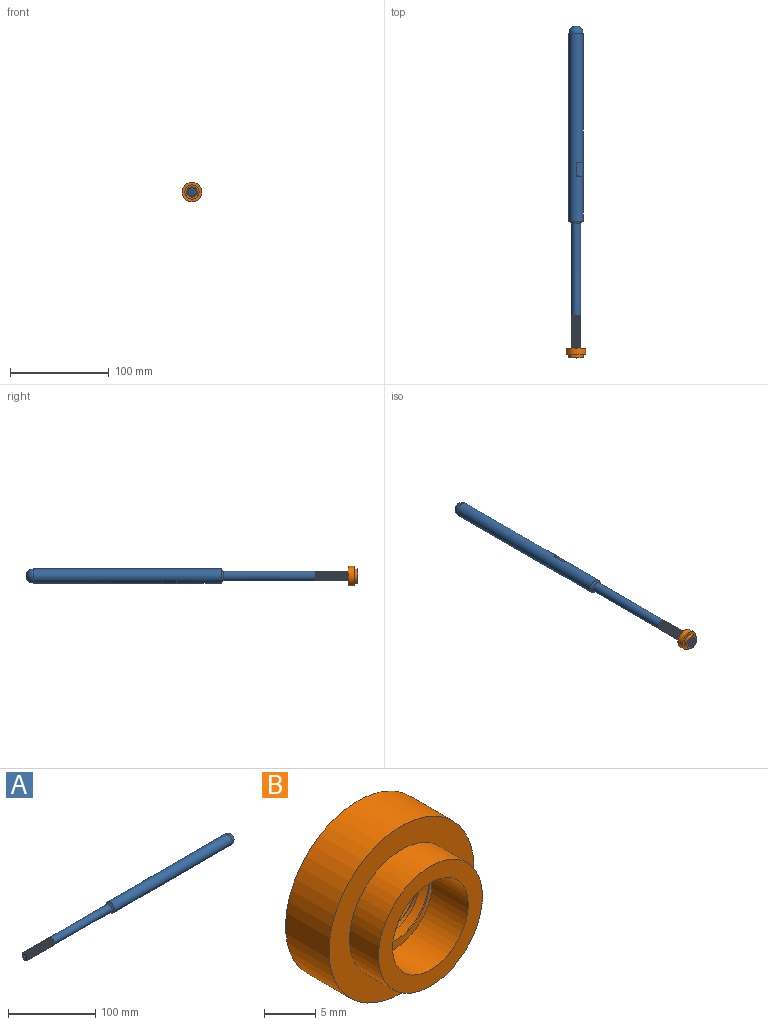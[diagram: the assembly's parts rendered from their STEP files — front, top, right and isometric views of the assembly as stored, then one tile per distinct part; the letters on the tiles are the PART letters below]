
ASSEMBLY  parts=2 mates=1
PART A: 68 faces, bbox 338x18x18 mm
  f0: cylinder r=7.15mm len=190.86mm, axis (-1,0,0), area 8339.1mm2, adj f1,f7,f8,f9,f10,f16,f17,f18
  f1: cylinder r=2.59mm len=3.79mm, axis (0,0,-1), area 0.2mm2, adj f0,f2,f9
  f2: plane 5.59x5.59mm, normal (0,0,-1), area 6.9mm2, adj f1,f3,f5,f6,f7,f8,f9
  f3: bspline ~8.22x5.92mm, area 60.7mm2, adj f2,f4,f5,f9
  f4: plane 4.64x4.63mm, normal (0,0,-1), area 14.3mm2, adj f3,f5,f6,f9
  f5: cylinder r=1.75mm len=7.15mm, axis (0,0,-1), area 19.5mm2, adj f2,f3,f4,f6
  f6: bspline ~8.22x5.92mm, area 60.7mm2, adj f2,f4,f5,f9
  f7: cylinder r=2.59mm len=5.19mm, axis (0,0,-1), area 0mm2, adj f0,f2
  f8: cylinder r=2.59mm len=4.13mm, axis (0,0,-1), area 0.9mm2, adj f0,f2,f9
  f9: bspline ~7.69x6.07mm, area 16.4mm2, adj f0,f1,f2,f3,f4,f6,f8
  f10: cylinder r=2.59mm len=3.79mm, axis (0,0,-1), area 0.2mm2, adj f0,f11,f18
  f11: plane 5.59x5.59mm, normal (0,0,-1), area 6.9mm2, adj f10,f12,f14,f15,f16,f17,f18
  f12: bspline ~8.22x5.92mm, area 60.7mm2, adj f11,f13,f14,f18
  f13: plane 4.64x4.63mm, normal (0,0,-1), area 14.3mm2, adj f12,f14,f15,f18
  f14: cylinder r=1.75mm len=7.15mm, axis (0,0,-1), area 19.5mm2, adj f11,f12,f13,f15
  f15: bspline ~8.22x5.92mm, area 60.7mm2, adj f11,f13,f14,f18
  f16: cylinder r=2.59mm len=5.19mm, axis (0,0,-1), area 0mm2, adj f0,f11
  f17: cylinder r=2.59mm len=4.13mm, axis (0,0,-1), area 0.9mm2, adj f0,f11,f18
  f18: bspline ~7.69x6.07mm, area 16.4mm2, adj f0,f10,f11,f12,f13,f15,f17
  f19: bspline ~6.29x4.05mm, area 3.6mm2, adj f0,f22
  f20: plane 0.78x0.45mm, normal (1,0,0), area 0mm2, adj f0,f21
  f21: bspline ~6.28x4.03mm, area 4mm2, adj f0,f20,f22
  f22: plane 13.19x5.39mm, normal (0,-0.87,-0.5), area 82.1mm2, adj f0,f19,f21
  f23: sphere r=7.15mm, area 320.8mm2, adj f0
  f24: bspline ~5.73x3.72mm, area 5.6mm2, adj f0,f67
  f25: plane 14.29x14.29mm, normal (-1,0,0), area 6.4mm2, adj f0,f26
  f26: torus R=7mm, axis (-1,0,0), area 113mm2, adj f25,f27
  f27: cylinder r=5mm len=95.5mm, axis (-1,0,0), area 2949mm2, adj f26,f28,f62,f63,f64,f65
  f28: bspline ~43.47x11.55mm, area 773.6mm2, adj f27,f29,f33,f35,f36,f37,f38,f39
  f29: plane 9.49x9.49mm, normal (-1,0,0), area 54.6mm2, adj f28,f30,f31,f33,f61
  f30: bspline ~42.72x11.55mm, area 756.9mm2, adj f29,f33,f35,f36,f37,f38,f39,f40
  f31: cylinder r=1.8mm len=3.6mm, axis (-1,0,0), area 29.4mm2, adj f29,f32
  f32: plane 3.6x3.6mm, normal (-1,0,0), area 10.2mm2, adj f31
  f33: bspline ~43.13x9.67mm, area 308.2mm2, adj f28,f29,f30,f34
  f34: bspline ~9.37x9mm, area 11.9mm2, adj f33,f63,f64,f65
  f35: cylinder r=5mm len=10mm, axis (-1,0,0), area 5.9mm2, adj f28,f30,f36,f62
  f36: cylinder r=5mm len=10mm, axis (-1,0,0), area 5.9mm2, adj f28,f30,f35,f37
  f37: cylinder r=5mm len=10mm, axis (-1,0,0), area 5.9mm2, adj f28,f30,f36,f38
  f38: cylinder r=5mm len=10mm, axis (-1,0,0), area 5.9mm2, adj f28,f30,f37,f39
  f39: cylinder r=5mm len=10mm, axis (-1,0,0), area 5.9mm2, adj f28,f30,f38,f40
  f40: cylinder r=5mm len=10mm, axis (-1,0,0), area 5.9mm2, adj f28,f30,f39,f41
  f41: cylinder r=5mm len=10mm, axis (-1,0,0), area 5.9mm2, adj f28,f30,f40,f42
  f42: cylinder r=5mm len=10mm, axis (-1,0,0), area 5.9mm2, adj f28,f30,f41,f43
  f43: cylinder r=5mm len=10mm, axis (-1,0,0), area 5.9mm2, adj f28,f30,f42,f44
  f44: cylinder r=5mm len=10mm, axis (-1,0,0), area 5.9mm2, adj f28,f30,f43,f45
  f45: cylinder r=5mm len=10mm, axis (-1,0,0), area 5.9mm2, adj f28,f30,f44,f46
  f46: cylinder r=5mm len=10mm, axis (-1,0,0), area 5.9mm2, adj f28,f30,f45,f47
  f47: cylinder r=5mm len=10mm, axis (-1,0,0), area 5.9mm2, adj f28,f30,f46,f48
  f48: cylinder r=5mm len=10mm, axis (-1,0,0), area 5.9mm2, adj f28,f30,f47,f49
  f49: cylinder r=5mm len=10mm, axis (-1,0,0), area 5.9mm2, adj f28,f30,f48,f50
  f50: cylinder r=5mm len=10mm, axis (-1,0,0), area 5.9mm2, adj f28,f30,f49,f51
  f51: cylinder r=5mm len=10mm, axis (-1,0,0), area 5.9mm2, adj f28,f30,f50,f52
  f52: cylinder r=5mm len=10mm, axis (-1,0,0), area 5.9mm2, adj f28,f30,f51,f53
  f53: cylinder r=5mm len=10mm, axis (-1,0,0), area 5.9mm2, adj f28,f30,f52,f54
  f54: cylinder r=5mm len=10mm, axis (-1,0,0), area 5.9mm2, adj f28,f30,f53,f55
  f55: cylinder r=5mm len=10mm, axis (-1,0,0), area 5.9mm2, adj f28,f30,f54,f56
  f56: cylinder r=5mm len=10mm, axis (-1,0,0), area 5.9mm2, adj f28,f30,f55,f57
  f57: cylinder r=5mm len=10mm, axis (-1,0,0), area 5.9mm2, adj f28,f30,f56,f58
  f58: cylinder r=5mm len=10mm, axis (-1,0,0), area 5.9mm2, adj f28,f30,f57,f59
  f59: cylinder r=5mm len=10mm, axis (-1,0,0), area 5.9mm2, adj f28,f30,f58,f60
  f60: cylinder r=5mm len=10mm, axis (-1,0,0), area 5.9mm2, adj f28,f30,f59,f61
  f61: cylinder r=5mm len=10mm, axis (-1,0,0), area 4.3mm2, adj f28,f29,f30,f60
  f62: cylinder r=5mm len=10mm, axis (-1,0,0), area 5.9mm2, adj f27,f28,f30,f35
  f63: bspline ~10.99x10.62mm, area 15mm2, adj f27,f30,f34,f64
  f64: plane 0.46x0.13mm, normal (0.01,0.5,-0.86), area 0mm2, adj f27,f34,f63,f65
  f65: bspline ~10.99x10.62mm, area 15mm2, adj f27,f28,f34,f64
  f66: bspline ~5.73x3.72mm, area 5.6mm2, adj f0,f67
  f67: plane 13.2x5.38mm, normal (0,0.87,0.5), area 82mm2, adj f0,f24,f66
PART B: 11 faces, bbox 20.4x11.2x20.4 mm
  f0: plane 20.44x20.44mm, normal (0,1,0), area 247.1mm2, adj f2,f7,f8,f9,f10
  f1: plane 10.88x10.88mm, normal (0,-1,0), area 18.6mm2, adj f6,f7,f8,f9,f10
  f2: cylinder r=10mm len=20mm, axis (0,1,0), area 377mm2, adj f0,f4
  f3: cylinder r=7.17mm len=14.35mm, axis (0,-1,0), area 180.3mm2, adj f4,f5
  f4: plane 20x20mm, normal (0,-1,0), area 152.4mm2, adj f2,f3
  f5: plane 14.35x14.35mm, normal (0,-1,0), area 76.1mm2, adj f3,f6
  f6: cylinder r=5.22mm len=10.44mm, axis (0,-1,0), area 164mm2, adj f1,f5
  f7: bspline ~11.69x10.12mm, area 91.2mm2, adj f0,f1,f9,f10
  f8: bspline ~11.69x10.12mm, area 91.5mm2, adj f0,f1,f9,f10
  f9: bspline ~11.85x10.26mm, area 23.2mm2, adj f0,f1,f7,f8
  f10: cylinder r=4.25mm len=8.5mm, axis (0,1,0), area 32.9mm2, adj f0,f1,f7,f8
PLACE A rot(axis=(-0.58,-0.58,0.58),120deg) t=(-17.38,62.56,10.5)mm
PLACE B t=(-17.38,1.72,-64.14)mm
MATE fastened A.f31 <-> B.f2  axis (0,-1,0) through (-17.38,-8.28,10.5)mm
